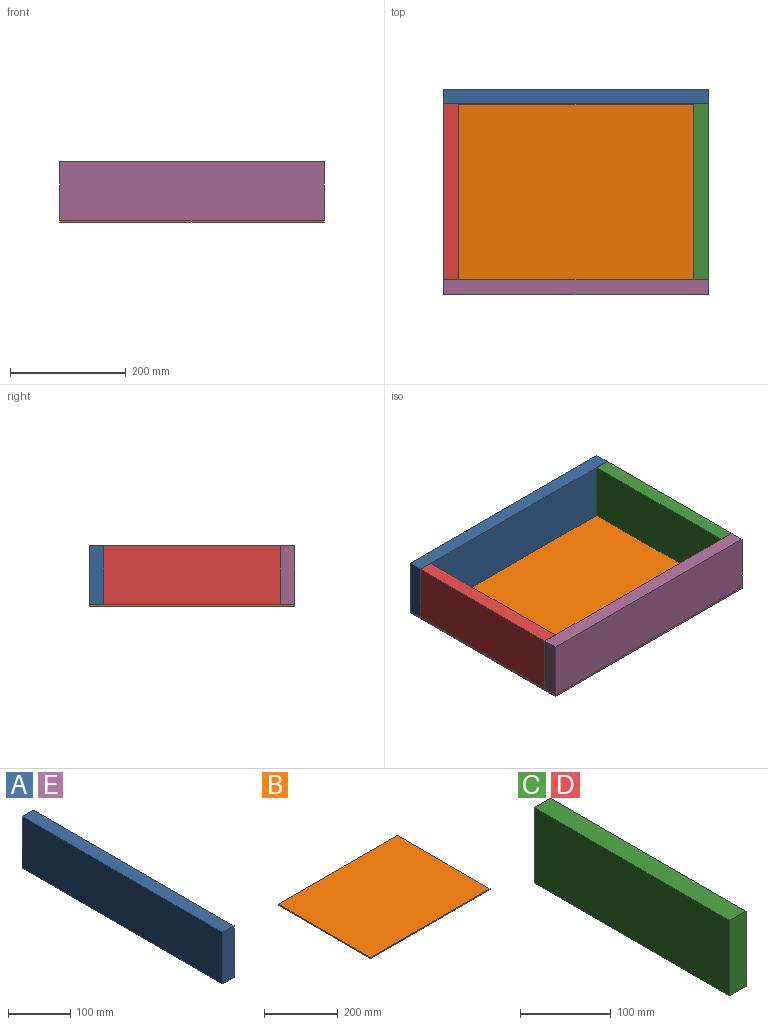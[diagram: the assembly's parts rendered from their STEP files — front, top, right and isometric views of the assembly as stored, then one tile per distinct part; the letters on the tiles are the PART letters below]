
ASSEMBLY  parts=5 mates=13
PART A: 6 faces, bbox 25.4x457.2x101.6 mm
  f0: plane 457.2x101.6mm, normal (-1,0,0), area 46451.5mm2, adj f1,f3,f4,f5
  f1: plane 457.2x25.4mm, normal (0,0,-1), area 11612.9mm2, adj f0,f2,f4,f5
  f2: plane 457.2x101.6mm, normal (1,0,0), area 46451.5mm2, adj f1,f3,f4,f5
  f3: plane 457.2x25.4mm, normal (0,0,1), area 11612.9mm2, adj f0,f2,f4,f5
  f4: plane 101.6x25.4mm, normal (0,-1,0), area 2580.6mm2, adj f0,f1,f2,f3
  f5: plane 101.6x25.4mm, normal (0,1,0), area 2580.6mm2, adj f0,f1,f2,f3
PART B: 6 faces, bbox 457.2x355.6x3.2 mm
  f0: plane 457.2x3.18mm, normal (0,1,0), area 1451.6mm2, adj f1,f3,f4,f5
  f1: plane 355.6x3.18mm, normal (-1,0,0), area 1129mm2, adj f0,f2,f4,f5
  f2: plane 457.2x3.18mm, normal (0,-1,0), area 1451.6mm2, adj f1,f3,f4,f5
  f3: plane 355.6x3.18mm, normal (1,0,0), area 1129mm2, adj f0,f2,f4,f5
  f4: plane 457.2x355.6mm, normal (0,0,-1), area 162580.3mm2, adj f0,f1,f2,f3
  f5: plane 457.2x355.6mm, normal (0,0,1), area 162580.3mm2, adj f0,f1,f2,f3
PART C: 6 faces, bbox 25.4x304.8x101.6 mm
  f0: plane 304.8x101.6mm, normal (-1,0,0), area 30967.7mm2, adj f1,f3,f4,f5
  f1: plane 304.8x25.4mm, normal (0,0,-1), area 7741.9mm2, adj f0,f2,f4,f5
  f2: plane 304.8x101.6mm, normal (1,0,0), area 30967.7mm2, adj f1,f3,f4,f5
  f3: plane 304.8x25.4mm, normal (0,0,1), area 7741.9mm2, adj f0,f2,f4,f5
  f4: plane 101.6x25.4mm, normal (0,-1,0), area 2580.6mm2, adj f0,f1,f2,f3
  f5: plane 101.6x25.4mm, normal (0,1,0), area 2580.6mm2, adj f0,f1,f2,f3
PART D: same geometry as C
PART E: same geometry as A
PLACE A rot(axis=(0,0,1),90deg) t=(0,0,0)mm
PLACE B at identity
PLACE C t=(431.8,0,0)mm
PLACE D at identity fixed
PLACE E rot(axis=(0,0,1),90deg) t=(0,-330.2,0)mm
MATE planar D.f1 <-> B.f5  axis (0,0,-1) through (12.7,-152.4,0)mm
MATE planar D.f3 <-> E.f3  axis (0,0,1) through (12.7,-152.4,101.6)mm
MATE planar E.f2 <-> D.f4  axis (0,1,0) through (228.6,-304.8,50.8)mm
MATE planar A.f0 <-> D.f5  axis (0,-1,0) through (228.6,0,50.8)mm
MATE planar A.f4 <-> C.f2  axis (1,0,0) through (457.2,12.7,50.8)mm
MATE planar E.f4 <-> C.f2  axis (1,0,0) through (457.2,-317.5,50.8)mm
MATE planar C.f3 <-> E.f3  axis (0,0,1) through (444.5,-152.4,101.6)mm
MATE planar D.f0 <-> E.f5  axis (-1,0,0) through (0,-152.4,50.8)mm
MATE planar A.f1 <-> B.f5  axis (0,0,-1) through (228.6,12.7,0)mm
MATE parallel E.f0 <-> D.f4  axis (0,-1,0) through (228.6,-330.2,50.8)mm
MATE planar A.f2 <-> B.f0  axis (0,1,0) through (228.6,25.4,50.8)mm
MATE planar D.f0 <-> B.f1  axis (-1,0,0) through (0,-152.4,50.8)mm
MATE planar C.f4 <-> E.f2  axis (0,-1,0) through (444.5,-304.8,50.8)mm
